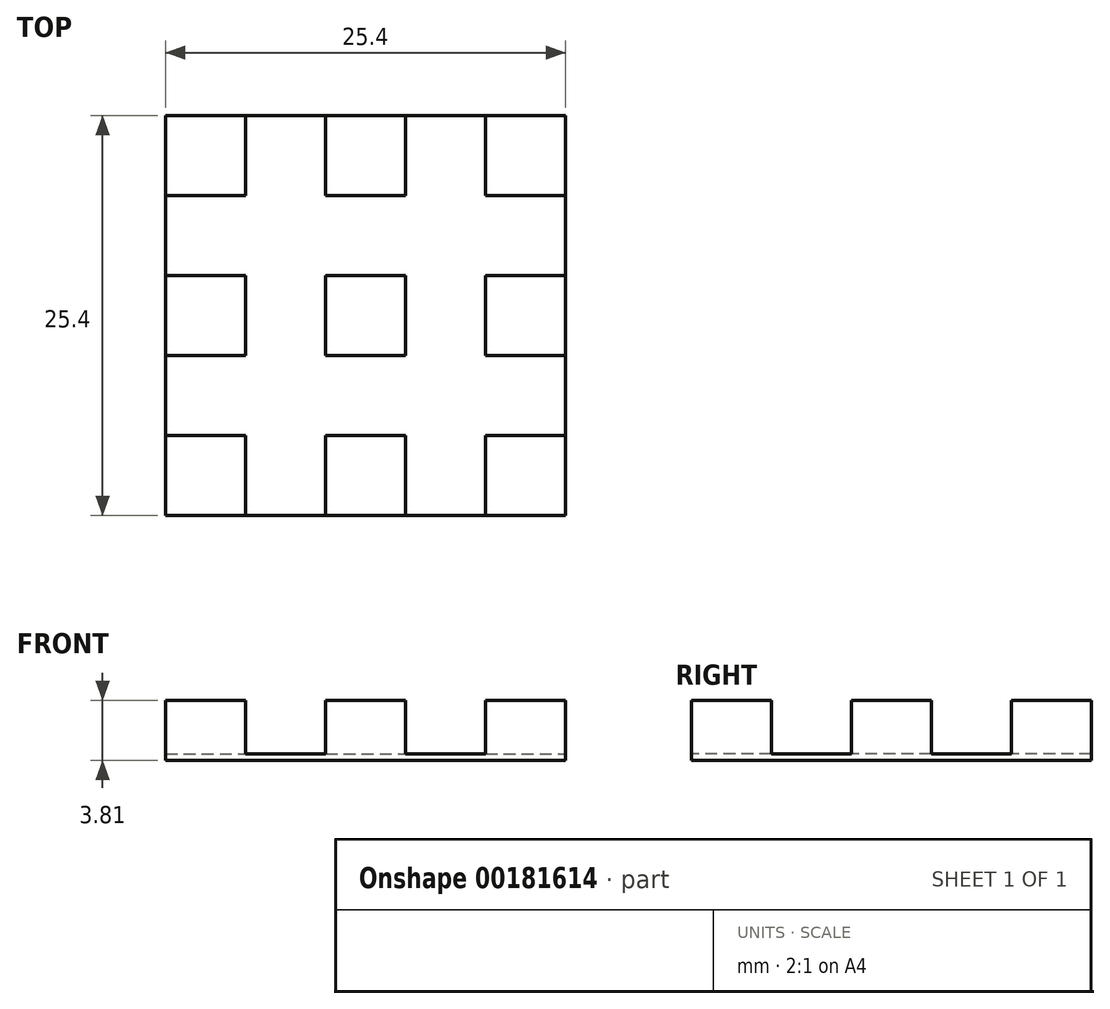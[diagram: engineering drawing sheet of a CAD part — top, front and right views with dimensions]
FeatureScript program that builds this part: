
annotation { "Feature Type Name" : "Feature", "Feature Type Description" : "" }
export const myFeature = defineFeature(function(context is Context, id is Id, definition is map)
    precondition{}
    {
        {
            var Q0;
            Q0=qCreatedBy(makeId("Top.planeOp"),FACE);
            var sketch = newSketch(context, id + "F0", { "sketchPlane" : qUnion([Q0])});
            skLineSegment(sketch, "E0.bottom", {"start": v(-12.7, 12.7) * mm, "end": v(12.7, 12.7) * mm});
            skLineSegment(sketch, "E0.top", {"start": v(-12.7, -12.7) * mm, "end": v(12.7, -12.7) * mm});
            skLineSegment(sketch, "E0.left", {"start": v(-12.7, 12.7) * mm, "end": v(-12.7, -12.7) * mm});
            skLineSegment(sketch, "E0.right", {"start": v(12.7, 12.7) * mm, "end": v(12.7, -12.7) * mm});
            skLineSegment(sketch, "E1.0", {"start": v(-7.62, 12.7) * mm, "end": v(-7.62, 7.62) * mm});
            skLineSegment(sketch, "E2.0", {"start": v(7.62, 12.7) * mm, "end": v(7.62, 7.62) * mm});
            skLineSegment(sketch, "E3.0", {"start": v(2.54, 12.7) * mm, "end": v(2.54, 7.62) * mm});
            skLineSegment(sketch, "E4.0", {"start": v(-2.54, 12.7) * mm, "end": v(-2.54, 7.62) * mm});
            skLineSegment(sketch, "E5.0", {"start": v(-12.7, 7.62) * mm, "end": v(-7.62, 7.62) * mm});
            skLineSegment(sketch, "E6.0", {"start": v(-12.7, 2.54) * mm, "end": v(-7.62, 2.54) * mm});
            skLineSegment(sketch, "E7.0", {"start": v(-12.7, -7.62) * mm, "end": v(-7.62, -7.62) * mm});
            skLineSegment(sketch, "E8.0", {"start": v(-12.7, -2.54) * mm, "end": v(-7.62, -2.54) * mm});
            skLineSegment(sketch, "E9.trimOffspring", {"start": v(-7.62, -7.62) * mm, "end": v(-7.62, -12.7) * mm});
            skLineSegment(sketch, "E10.trimOffspring", {"start": v(-2.54, -7.62) * mm, "end": v(2.54, -7.62) * mm});
            skLineSegment(sketch, "E11.trimOffspring", {"start": v(-2.54, -7.62) * mm, "end": v(-2.54, -12.7) * mm});
            skLineSegment(sketch, "E12.trimOffspring", {"start": v(-2.54, -2.54) * mm, "end": v(2.54, -2.54) * mm});
            skLineSegment(sketch, "E13.trimOffspring", {"start": v(-2.54, 2.54) * mm, "end": v(2.54, 2.54) * mm});
            skLineSegment(sketch, "E14.trimOffspring", {"start": v(-7.62, 2.54) * mm, "end": v(-7.62, -2.54) * mm});
            skLineSegment(sketch, "E15.trimOffspring", {"start": v(-2.54, 7.62) * mm, "end": v(2.54, 7.62) * mm});
            skLineSegment(sketch, "E16.trimOffspring", {"start": v(-2.54, 2.54) * mm, "end": v(-2.54, -2.54) * mm});
            skLineSegment(sketch, "E17.trimOffspring", {"start": v(2.54, 2.54) * mm, "end": v(2.54, -2.54) * mm});
            skLineSegment(sketch, "E18.trimOffspring", {"start": v(7.62, 7.62) * mm, "end": v(12.7, 7.62) * mm});
            skLineSegment(sketch, "E19.trimOffspring", {"start": v(7.62, 2.54) * mm, "end": v(7.62, -2.54) * mm});
            skLineSegment(sketch, "E20.trimOffspring", {"start": v(7.62, 2.54) * mm, "end": v(12.7, 2.54) * mm});
            skLineSegment(sketch, "E21.trimOffspring", {"start": v(7.62, -2.54) * mm, "end": v(12.7, -2.54) * mm});
            skLineSegment(sketch, "E22.trimOffspring", {"start": v(7.62, -7.62) * mm, "end": v(7.62, -12.7) * mm});
            skLineSegment(sketch, "E23.trimOffspring", {"start": v(7.62, -7.62) * mm, "end": v(12.7, -7.62) * mm});
            skLineSegment(sketch, "E24.trimOffspring", {"start": v(2.54, -7.62) * mm, "end": v(2.54, -12.7) * mm});
            skSolve(sketch);
        }
        {
            var Q0;
            {var subQ13=sQuery(id+"F0.wireOp",EDGE,"E1.0");Q0=makeQuery(id+"F0.imprint","IMPRINT",FACE,{"disambiguationData":[TD([[makeQuery(id+"F0.imprint","IMPRINT",EDGE,{"derivedFrom":subQ13}),1.0]])]});}
            extrude(context, id + "F1", {"entities" : qUnion([Q0]), "depth" : 0.4 * mm, "offsetDistance" : 25.4 * mm});
        }
        {
            var Q0;
            {var subQ4=sQuery(id+"F0.wireOp",EDGE,"E7.0");Q0=makeQuery(id+"F0.imprint","IMPRINT",FACE,{"disambiguationData":[TD([[makeQuery(id+"F0.imprint","IMPRINT",EDGE,{"derivedFrom":subQ4}),-1.0]])]});}
            var Q1;
            {var subQ0=sQuery(id+"F0.wireOp",EDGE,"E6.0");Q1=makeQuery(id+"F0.imprint","IMPRINT",FACE,{"disambiguationData":[TD([[makeQuery(id+"F0.imprint","IMPRINT",EDGE,{"derivedFrom":subQ0}),-1.0]])]});}
            var Q2;
            {var subQ3=sQuery(id+"F0.wireOp",EDGE,"E1.0");Q2=makeQuery(id+"F0.imprint","IMPRINT",FACE,{"disambiguationData":[TD([[makeQuery(id+"F0.imprint","IMPRINT",EDGE,{"derivedFrom":subQ3}),-1.0]])]});}
            var Q3;
            {var subQ0=sQuery(id+"F0.wireOp",EDGE,"E3.0");Q3=makeQuery(id+"F0.imprint","IMPRINT",FACE,{"disambiguationData":[TD([[makeQuery(id+"F0.imprint","IMPRINT",EDGE,{"derivedFrom":subQ0}),-1.0]])]});}
            var Q4;
            Q4=makeQuery(id+"F0.imprint","IMPRINT",FACE,{"disambiguationData":[TD([[makeQuery(id+"F0.imprint","IMPRINT",EDGE,{"derivedFrom":sQuery(id+"F0.wireOp",EDGE,"E12.trimOffspring")}),1.0]])]});
            var Q5;
            Q5=makeQuery(id+"F0.imprint","IMPRINT",FACE,{"disambiguationData":[TD([[makeQuery(id+"F0.imprint","IMPRINT",EDGE,{"derivedFrom":sQuery(id+"F0.wireOp",EDGE,"E19.trimOffspring")}),1.0]])]});
            var Q6;
            {var subQ3=sQuery(id+"F0.wireOp",EDGE,"E2.0");Q6=makeQuery(id+"F0.imprint","IMPRINT",FACE,{"disambiguationData":[TD([[makeQuery(id+"F0.imprint","IMPRINT",EDGE,{"derivedFrom":subQ3}),1.0]])]});}
            var Q7;
            {var subQ3=sQuery(id+"F0.wireOp",EDGE,"E22.trimOffspring");Q7=makeQuery(id+"F0.imprint","IMPRINT",FACE,{"disambiguationData":[TD([[makeQuery(id+"F0.imprint","IMPRINT",EDGE,{"derivedFrom":subQ3}),1.0]])]});}
            var Q8;
            Q8=makeQuery(id+"F0.imprint","IMPRINT",FACE,{"disambiguationData":[TD([[makeQuery(id+"F0.imprint","IMPRINT",EDGE,{"derivedFrom":sQuery(id+"F0.wireOp",EDGE,"E10.trimOffspring")}),-1.0]])]});
            extrude(context, id + "F2", {"entities" : qUnion([Q0, Q1, Q2, Q3, Q4, Q5, Q6, Q7, Q8]), "operationType" : NewBodyOperationType.ADD, "depth" : 3.8 * mm, "offsetDistance" : 25.4 * mm});
        }
    });
